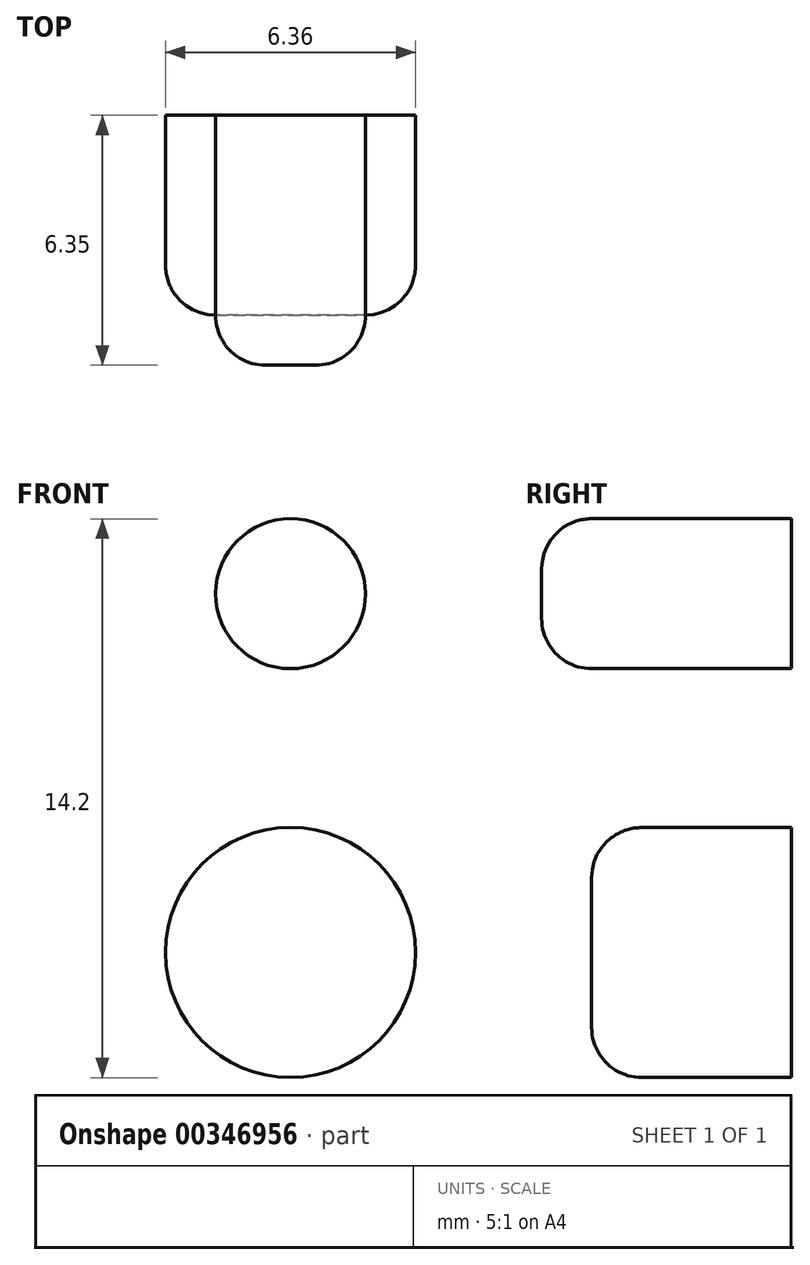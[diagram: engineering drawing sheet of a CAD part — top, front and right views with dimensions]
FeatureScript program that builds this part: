
annotation { "Feature Type Name" : "Feature", "Feature Type Description" : "" }
export const myFeature = defineFeature(function(context is Context, id is Id, definition is map)
    precondition{}
    {
        {
            var Q0;
            Q0=qCreatedBy(makeId("Front.planeOp"),FACE);
            var sketch = newSketch(context, id + "F0", { "sketchPlane" : qUnion([Q0])});
            skCircle(sketch, "E0", {"center": v(0, 0) * mm, "radius": 3.18 * mm});
            skSolve(sketch);
        }
        {
            var Q0;
            Q0=makeQuery(id+"F0.imprint","IMPRINT",FACE,{"disambiguationData":[TD([[makeQuery(id+"F0.imprint","IMPRINT",EDGE,{"derivedFrom":sQuery(id+"F0.wireOp",EDGE,"E0")}),1.0]])]});
            extrude(context, id + "F1", {"entities" : qUnion([Q0]), "depth" : 5.08 * mm});
        }
        {
            var Q0;
            Q0=makeQuery(id+"F1.opExtrude","CAP_EDGE",EDGE,{"disambiguationData":[OSD([sQuery(id+"F0.wireOp",EDGE,"E0")])],"isStart":false});
            fillet(context, id + "F2", {"entities" : qUnion([Q0]), "radius" : 1.27 * mm, "tangentPropagation" : true, "allowEdgeOverflow" : false});
        }
        {
            var Q0;
            Q0=qCreatedBy(makeId("Front.planeOp"),FACE);
            var sketch = newSketch(context, id + "F3", { "sketchPlane" : qUnion([Q0])});
            skCircle(sketch, "E1", {"center": v(0, 9.12) * mm, "radius": 1.9 * mm});
            skSolve(sketch);
        }
        {
            var Q0;
            Q0=makeQuery(id+"F3.imprint","IMPRINT",FACE,{"disambiguationData":[TD([[makeQuery(id+"F3.imprint","IMPRINT",EDGE,{"derivedFrom":sQuery(id+"F3.wireOp",EDGE,"E1")}),1.0]])]});
            extrude(context, id + "F4", {"entities" : qUnion([Q0]), "depth" : 6.35 * mm});
        }
        {
            var Q0;
            Q0=makeQuery(id+"F4.opExtrude","CAP_EDGE",EDGE,{"disambiguationData":[OSD([sQuery(id+"F3.wireOp",EDGE,"E1")])],"isStart":false});
            fillet(context, id + "F5", {"entities" : qUnion([Q0]), "radius" : 1.27 * mm, "tangentPropagation" : true, "allowEdgeOverflow" : false});
        }
    });
